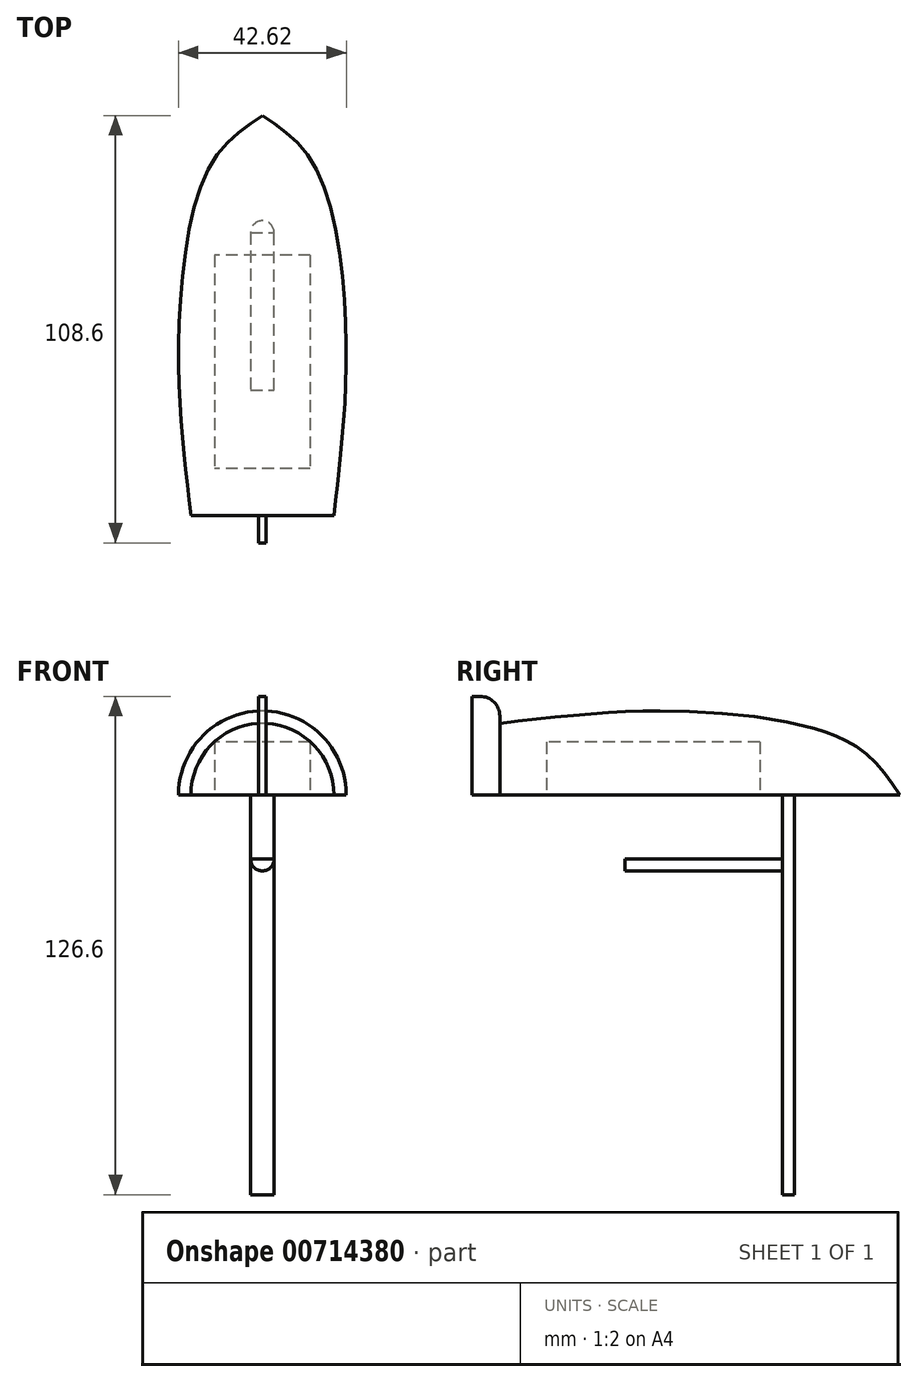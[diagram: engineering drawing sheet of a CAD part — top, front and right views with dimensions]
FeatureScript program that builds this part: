
annotation { "Feature Type Name" : "Feature", "Feature Type Description" : "" }
export const myFeature = defineFeature(function(context is Context, id is Id, definition is map)
    precondition{}
    {
        {
            var Q0;
            Q0=qCreatedBy(makeId("Top.planeOp"),FACE);
            var sketch = newSketch(context, id + "F0", { "sketchPlane" : qUnion([Q0])});
            skFitSpline(sketch, "E0", {"points": [v(0, 101.6) * mm, v(13.48, 88.44) * mm, v(21.13, 49.36) * mm, v(20.28, 19.64) * mm, v(18.15, 0) * mm], "startDerivative": vector(70.82, -47.26) * mm, "endDerivative": vector(-10.4, -87.77) * mm});
            skLineSegment(sketch, "E1", {"start": v(0, 101.6) * mm, "end": v(0, 0) * mm});
            skLineSegment(sketch, "E2", {"start": v(0, 0) * mm, "end": v(18.15, 0) * mm});
            skSolve(sketch);
        }
        {
            var Q0;
            Q0=makeQuery(id+"F0.imprint","IMPRINT",FACE,{"disambiguationData":[TD([[makeQuery(id+"F0.imprint","IMPRINT",EDGE,{"derivedFrom":sQuery(id+"F0.wireOp",EDGE,"E0")}),-1.0]])]});
            var Q1;
            Q1=sQuery(id+"F0.wireOp",EDGE,"E1");
            revolve(context, id + "F1", {"surfaceOperationType" : NewSurfaceOperationType.NEW, "entities" : qUnion([Q0]), "axis" : qUnion([Q1]), "revolveType" : RevolveType.ONE_DIRECTION, "angle" : 180 * degree});
        }
        {
            var Q0;
            Q0=makeQuery(id+"F1.opRevolve","SWEPT_FACE",FACE,{"disambiguationData":[OSD([sQuery(id+"F0.wireOp",EDGE,"E2")])]});
            var sketch = newSketch(context, id + "F2", { "sketchPlane" : qUnion([Q0])});
            skLineSegment(sketch, "E3", {"start": v(-0.97, 0) * mm, "end": v(0.97, 0) * mm});
            skLineSegment(sketch, "E4", {"start": v(0.97, 0) * mm, "end": v(0.97, 25) * mm});
            skLineSegment(sketch, "E5", {"start": v(-0.97, 0) * mm, "end": v(-0.97, 25) * mm});
            skLineSegment(sketch, "E6", {"start": v(-0.97, 25) * mm, "end": v(0.97, 25) * mm});
            skSolve(sketch);
        }
        {
            var Q0;
            {var subQ0=sQuery(id+"F2.wireOp",EDGE,"E3");Q0=makeQuery(id+"F2.imprint","IMPRINT",FACE,{"disambiguationData":[TD([[makeQuery(id+"F2.imprint","IMPRINT",EDGE,{"derivedFrom":subQ0}),-1.0]])]});}
            var Q1;
            {var subQ0=sQuery(id+"F2.wireOp",EDGE,"E6");Q1=makeQuery(id+"F2.imprint","IMPRINT",FACE,{"disambiguationData":[TD([[makeQuery(id+"F2.imprint","IMPRINT",EDGE,{"derivedFrom":subQ0}),-1.0]])]});}
            extrude(context, id + "F3", {"entities" : qUnion([Q0, Q1]), "operationType" : NewBodyOperationType.ADD, "depth" : 7 * mm, "offsetDistance" : 25 * mm});
        }
        {
            var Q0;
            Q0=makeQuery(id+"F3.opExtrude","CAP_EDGE",EDGE,{"disambiguationData":[OSD([sQuery(id+"F2.wireOp",EDGE,"E6")])],"isStart":true});
            fillet(context, id + "F4", {"entities" : qUnion([Q0]), "radius" : 5 * mm, "tangentPropagation" : true, "allowEdgeOverflow" : false});
        }
        {
            var Q0;
            Q0=makeQuery(id+"F3.boolean.opBoolean","MERGE",FACE,{"derivedFrom":[makeQuery(id+"F1.opRevolve","CAP_FACE",FACE,{"disambiguationData":[OSD([sQuery(id+"F0.wireOp",EDGE,"E0"),sQuery(id+"F0.wireOp",EDGE,"E1"),sQuery(id+"F0.wireOp",EDGE,"E2")])],"isStart":false}),makeQuery(id+"F3.opExtrude","SWEPT_FACE",FACE,{"disambiguationData":[OSD([sQuery(id+"F2.wireOp",EDGE,"E3")])]})]});
            var sketch = newSketch(context, id + "F5", { "sketchPlane" : qUnion([Q0])});
            skLineSegment(sketch, "E7", {"start": v(0, -71.83) * mm, "end": v(3, -71.83) * mm});
            skLineSegment(sketch, "E8", {"start": v(0, -71.83) * mm, "end": v(-3, -71.83) * mm});
            skArc(sketch, "E9", {"start": v(-3, -71.83) * mm, "mid": v(0, -74.83) * mm, "end": v(3, -71.83) * mm});
            skSolve(sketch);
        }
        {
            var Q0;
            Q0=makeQuery(id+"F5.imprint","IMPRINT",FACE,{"disambiguationData":[TD([[makeQuery(id+"F5.imprint","IMPRINT",EDGE,{"derivedFrom":sQuery(id+"F5.wireOp",EDGE,"E7")}),-1.0]])]});
            extrude(context, id + "F6", {"entities" : qUnion([Q0]), "operationType" : NewBodyOperationType.ADD, "depth" : 101.6 * mm, "offsetDistance" : 25 * mm});
        }
        {
            var Q0;
            Q0=makeQuery(id+"F6.opExtrude","SWEPT_FACE",FACE,{"disambiguationData":[OSD([sQuery(id+"F5.wireOp",EDGE,"E7"),sQuery(id+"F5.wireOp",EDGE,"E8")])]});
            var sketch = newSketch(context, id + "F7", { "sketchPlane" : qUnion([Q0])});
            skLineSegment(sketch, "E10", {"start": v(-3, -16.34) * mm, "end": v(3, -16.34) * mm});
            skArc(sketch, "E11", {"start": v(-3, -16.34) * mm, "mid": v(0, -19.35) * mm, "end": v(3, -16.34) * mm});
            skSolve(sketch);
        }
        {
            var Q0;
            {var subQ0=sQuery(id+"F7.wireOp",EDGE,"E10");Q0=makeQuery(id+"F7.imprint","IMPRINT",FACE,{"disambiguationData":[TD([[makeQuery(id+"F7.imprint","IMPRINT",EDGE,{"derivedFrom":subQ0}),-1.0]])]});}
            extrude(context, id + "F8", {"entities" : qUnion([Q0]), "depth" : 40 * mm, "offsetDistance" : 25 * mm});
        }
        {
            var Q0;
            Q0=makeQuery(id+"F3.boolean.opBoolean","MERGE",FACE,{"derivedFrom":[makeQuery(id+"F1.opRevolve","CAP_FACE",FACE,{"disambiguationData":[OSD([sQuery(id+"F0.wireOp",EDGE,"E0"),sQuery(id+"F0.wireOp",EDGE,"E1"),sQuery(id+"F0.wireOp",EDGE,"E2")])],"isStart":false}),makeQuery(id+"F3.opExtrude","SWEPT_FACE",FACE,{"disambiguationData":[OSD([sQuery(id+"F2.wireOp",EDGE,"E3")])]})]});
            var sketch = newSketch(context, id + "F9", { "sketchPlane" : qUnion([Q0])});
            skLineSegment(sketch, "E12.bottom", {"start": v(12.13, -66.05) * mm, "end": v(-12.13, -66.05) * mm});
            skLineSegment(sketch, "E12.top", {"start": v(12.13, -11.9) * mm, "end": v(-12.13, -11.9) * mm});
            skLineSegment(sketch, "E12.left", {"start": v(12.13, -66.05) * mm, "end": v(12.13, -11.9) * mm});
            skLineSegment(sketch, "E12.right", {"start": v(-12.13, -66.05) * mm, "end": v(-12.13, -11.9) * mm});
            skSolve(sketch);
        }
        {
            var Q0;
            Q0=makeQuery(id+"F9.imprint","IMPRINT",FACE,{"disambiguationData":[TD([[makeQuery(id+"F9.imprint","IMPRINT",EDGE,{"derivedFrom":sQuery(id+"F9.wireOp",EDGE,"E12.bottom")}),-1.0]])]});
            extrude(context, id + "F10", {"entities" : qUnion([Q0]), "operationType" : NewBodyOperationType.REMOVE, "oppositeDirection" : true, "depth" : 13.4 * mm, "offsetDistance" : 25 * mm});
        }
    });
